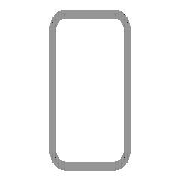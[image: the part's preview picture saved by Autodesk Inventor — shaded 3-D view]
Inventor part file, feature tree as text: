
AUTODESK INVENTOR PART (.ipt)
format: ipt  version: 2025.3 (Build 293356000, 356)  size: 149,504 bytes
history: native  units: mm (DEFAULTED — no unit token found)
features: other x4, plane x3, split x2, sketch x1
ambient origin geometry x8: Origin, YZ Plane, XZ Plane, XY Plane, X Axis, Y Axis, Z Axis, Center Point
bodies: Solid1 (feature_tree), Body (feature_tree)
feature tree (10):
  parser-record x1  (decoder bookkeeping rows leaked as tree rows — omitted from the tree; the rows remain in map.json)
  other  "Driven Length"
  other  "Start Plane"
  other  "End Plane"
  plane  "Work Plane4"
  split  "Split1"
  plane  "Work Plane5"
  split  "Split2"
  sketch  "Sketch3"  dims[d3=994.526745mm d4=0.0mm d7=6.0mm d9=40.0mm d11=80.0mm d12=3.0mm d13=33.685971mm d14=1028.212716mm d15=20.0mm d16=40.0mm d17=90.0deg d18=994.526745mm]
  plane  "Work Plane3"
